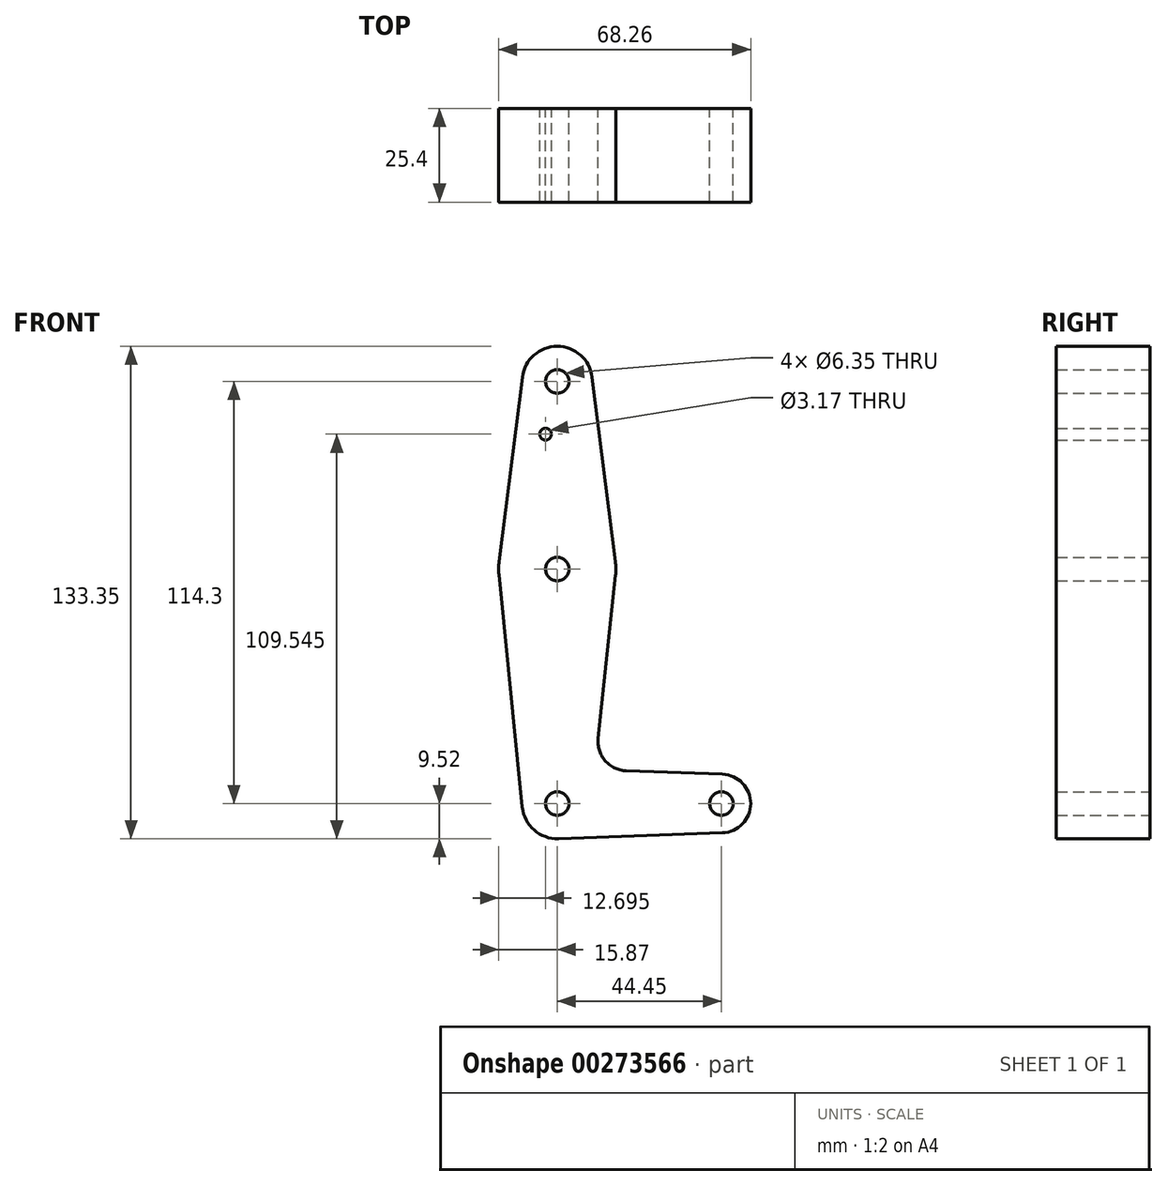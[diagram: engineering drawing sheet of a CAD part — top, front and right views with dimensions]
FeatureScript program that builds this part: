
annotation { "Feature Type Name" : "Feature", "Feature Type Description" : "" }
export const myFeature = defineFeature(function(context is Context, id is Id, definition is map)
    precondition{}
    {
        {
            var Q0;
            Q0=qCreatedBy(makeId("Front.planeOp"),FACE);
            var sketch = newSketch(context, id + "F0", { "sketchPlane" : qUnion([Q0])});
            skCircle(sketch, "E0", {"center": v(0, 114.3) * mm, "radius": 9.53 * mm});
            skCircle(sketch, "E1", {"center": v(0, 63.5) * mm, "radius": 15.88 * mm});
            skCircle(sketch, "E2", {"center": v(0, 0) * mm, "radius": 9.53 * mm});
            skCircle(sketch, "E3", {"center": v(44.45, 0) * mm, "radius": 7.94 * mm});
            skLineSegment(sketch, "E4", {"start": v(-9.45, 115.5) * mm, "end": v(-15.75, 65.48) * mm});
            skLineSegment(sketch, "E5", {"start": v(9.45, 115.5) * mm, "end": v(15.75, 65.48) * mm});
            skCircle(sketch, "E6", {"center": v(0, 114.3) * mm, "radius": 3.18 * mm});
            skCircle(sketch, "E7", {"center": v(0, 63.5) * mm, "radius": 3.18 * mm});
            skCircle(sketch, "E8", {"center": v(0, 0) * mm, "radius": 3.18 * mm});
            skCircle(sketch, "E9", {"center": v(44.45, 0) * mm, "radius": 3.18 * mm});
            skCircle(sketch, "E10", {"center": v(-3.18, 100.03) * mm, "radius": 1.59 * mm});
            skPoint(sketch, "E11.newPointB", {"position": v(0, 9.53) * mm});
            skLineSegment(sketch, "E12", {"start": v(-15.8, 61.91) * mm, "end": v(-9.48, -0.95) * mm});
            skLineSegment(sketch, "E13", {"start": v(0.34, -9.52) * mm, "end": v(44.73, -7.93) * mm});
            skLineSegment(sketch, "E14", {"start": v(44.73, 7.93) * mm, "end": v(18.68, 8.86) * mm});
            skLineSegment(sketch, "E15", {"start": v(15.78, 61.81) * mm, "end": v(11.06, 17.65) * mm});
            skArc(sketch, "E16.filletArc", {"start": v(11.06, 17.65) * mm, "mid": v(12.96, 11.6) * mm, "end": v(18.68, 8.86) * mm});
            skSolve(sketch);
        }
        {
            var Q0;
            Q0 = qSketchRegion(id + "F0", true);
            extrude(context, id + "F1", {"entities" : qUnion([Q0]), "depth" : 25.4 * mm});
        }
    });
